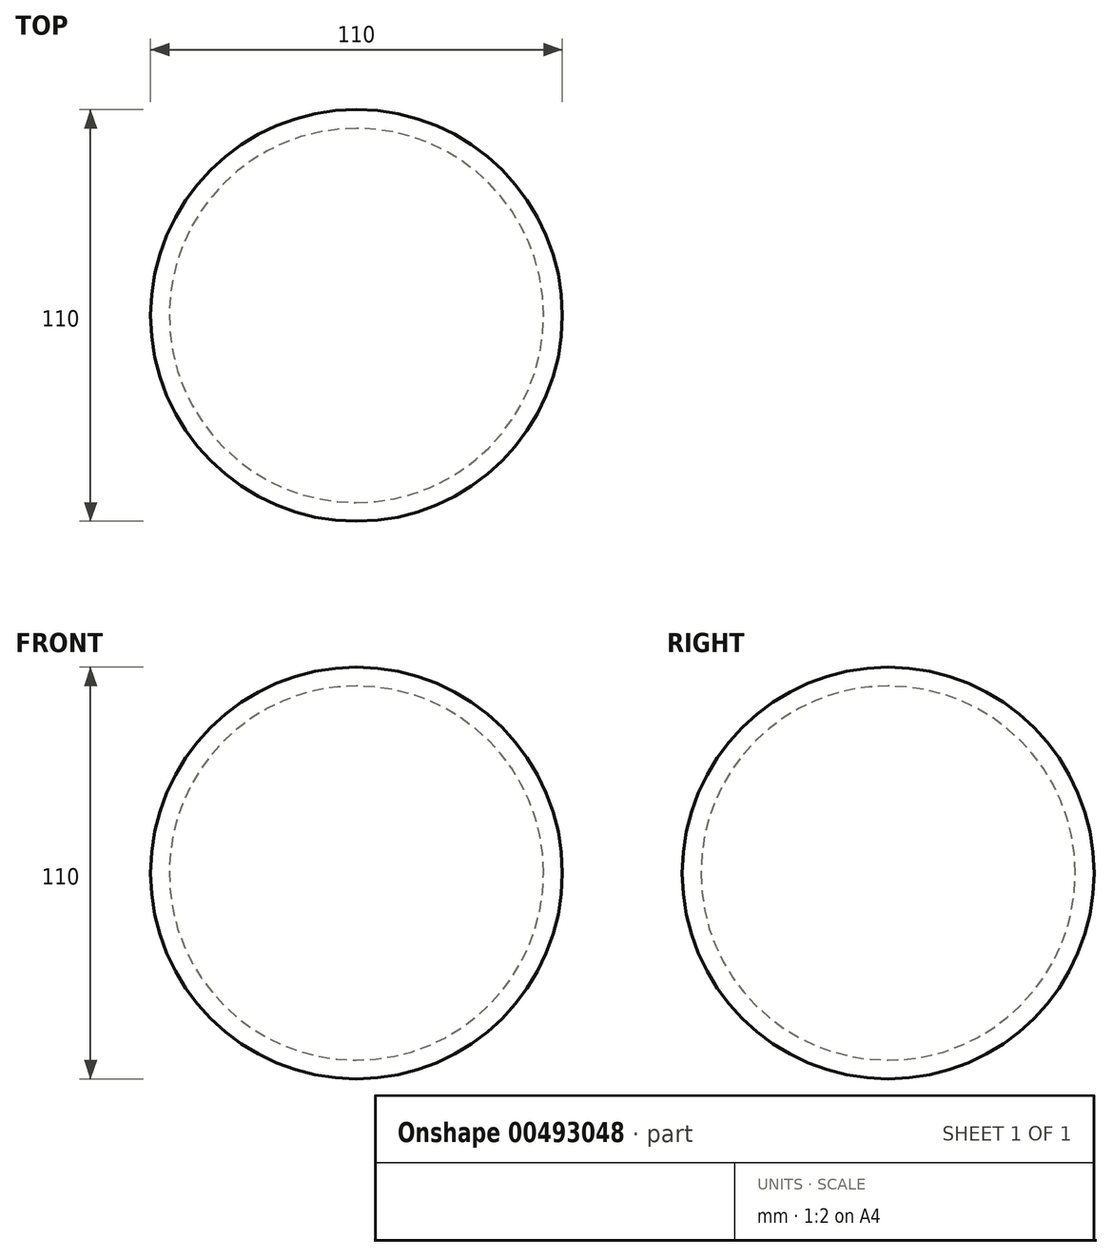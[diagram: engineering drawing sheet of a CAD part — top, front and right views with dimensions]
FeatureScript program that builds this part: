
annotation { "Feature Type Name" : "Feature", "Feature Type Description" : "" }
export const myFeature = defineFeature(function(context is Context, id is Id, definition is map)
    precondition{}
    {
        {
            var Q0;
            Q0=qCreatedBy(makeId("Front.planeOp"),FACE);
            var sketch = newSketch(context, id + "F0", { "sketchPlane" : qUnion([Q0])});
            skCircle(sketch, "E0", {"center": v(0, 0) * mm, "radius": 50 * mm});
            skSolve(sketch);
        }
        {
            var Q0;
            Q0=makeQuery(id+"F0.imprint","IMPRINT",FACE,{"disambiguationData":[TD([[makeQuery(id+"F0.imprint","IMPRINT",EDGE,{"derivedFrom":sQuery(id+"F0.wireOp",EDGE,"E0")}),1.0]])]});
            extrude(context, id + "F1", {"entities" : qUnion([Q0]), "depth" : 50 * mm, "hasSecondDirection" : true, "secondDirectionOppositeDirection" : true, "secondDirectionDepth" : 50 * mm});
        }
        {
            var Q0;
            Q0=makeQuery(id+"F6X7eB232KdeAEG_2.opExtrude","CAP_EDGE",EDGE,{"disambiguationData":[OSD([sQuery(id+"FETPKfv8dPtvasx_0.wireOp",EDGE,"071bc9c8-9610-47d9-8e70-59789fdb41a3")])],"isStart":true});
            var Q1;
            Q1=makeQuery(id+"F6X7eB232KdeAEG_2.opExtrude","CAP_EDGE",EDGE,{"disambiguationData":[OSD([sQuery(id+"FETPKfv8dPtvasx_0.wireOp",EDGE,"071bc9c8-9610-47d9-8e70-59789fdb41a3")])],"isStart":false});
            var Q2;
            Q2=makeQuery(id+"Fv94ot3d23qnKr2_1.opExtrude","CAP_EDGE",EDGE,{"disambiguationData":[OSD([sQuery(id+"FcYjKppYi7wfSge_0.wireOp",EDGE,"d14a3814-3a9e-4ba7-a8b5-343738211421")])],"isStart":false});
            var Q3;
            Q3=makeQuery(id+"F1.opExtrude","CAP_EDGE",EDGE,{"disambiguationData":[OSD([sQuery(id+"F0.wireOp",EDGE,"E0")])],"isStart":true});
            var Q4;
            Q4=makeQuery(id+"F1.opExtrude","CAP_EDGE",EDGE,{"disambiguationData":[OSD([sQuery(id+"F0.wireOp",EDGE,"E0")])],"isStart":false});
            var Q5;
            Q5=makeQuery(id+"Fv94ot3d23qnKr2_1.opExtrude","CAP_EDGE",EDGE,{"disambiguationData":[OSD([sQuery(id+"FcYjKppYi7wfSge_0.wireOp",EDGE,"d14a3814-3a9e-4ba7-a8b5-343738211421")])],"isStart":true});
            fillet(context, id + "F2", {"entities" : qUnion([Q0, Q1, Q2, Q3, Q4, Q5]), "radius" : 50 * mm, "tangentPropagation" : true, "allowEdgeOverflow" : false});
        }
        {
            var Q0;
            Q0=makeQuery(id+"F2.opFillet","BLEND_FACE",FACE,{"disambiguationData":[OSD([sQuery(id+"F0.wireOp",EDGE,"E0")])]});
            var Q1;
            Q1=makeQuery(id+"F1.opExtrude","SWEPT_BODY",BODY,{"disambiguationData":[OSD([sQuery(id+"F0.wireOp",EDGE,"E0")])]});
            shell(context, id + "F3", {"isHollow" : true, "entities" : qUnion([Q0]), "parts" : qUnion([Q1]), "thickness" : 5 * mm, "oppositeDirection" : true});
        }
    });
